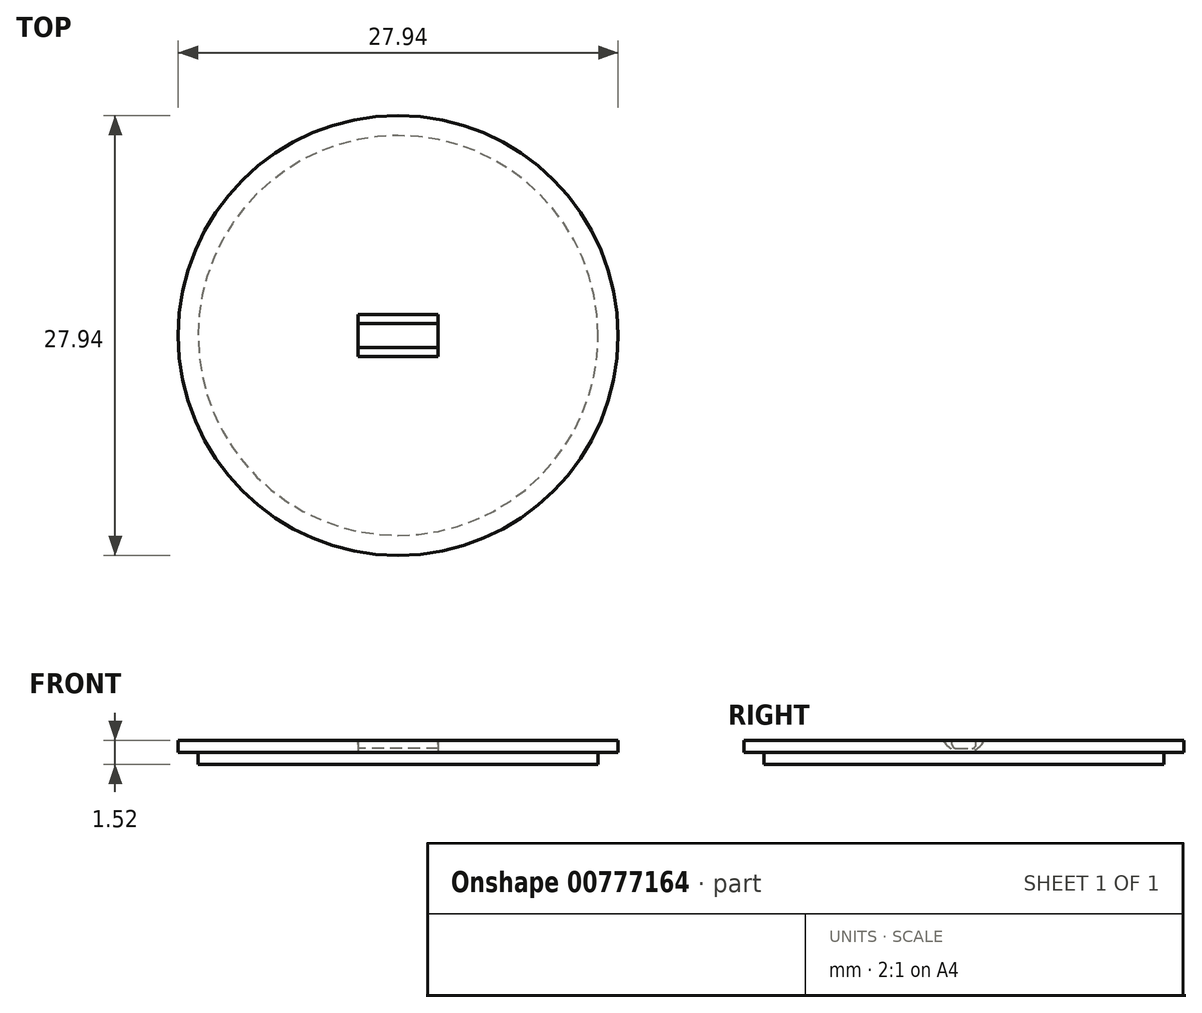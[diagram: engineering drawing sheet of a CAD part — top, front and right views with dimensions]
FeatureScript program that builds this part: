
annotation { "Feature Type Name" : "Feature", "Feature Type Description" : "" }
export const myFeature = defineFeature(function(context is Context, id is Id, definition is map)
    precondition{}
    {
        {
            var Q0;
            Q0=qCreatedBy(makeId("Top.planeOp"),FACE);
            var sketch = newSketch(context, id + "F0", { "sketchPlane" : qUnion([Q0])});
            skCircle(sketch, "E0", {"center": v(0, 0) * mm, "radius": 12.7 * mm});
            skSolve(sketch);
        }
        {
            var Q0;
            Q0=qSketchRegion(id+"F0",true);
            extrude(context, id + "F1", {"entities" : qUnion([Q0]), "oppositeDirection" : true, "depth" : 1.52 * mm, "offsetDistance" : 25.4 * mm});
        }
        {
            var Q0;
            Q0=qCreatedBy(makeId("Top.planeOp"),FACE);
            var sketch = newSketch(context, id + "F2", { "sketchPlane" : qUnion([Q0])});
            skCircle(sketch, "E1", {"center": v(0, 0) * mm, "radius": 13.97 * mm});
            skSolve(sketch);
        }
        {
            var Q0;
            Q0=qSketchRegion(id+"F2",true);
            extrude(context, id + "F3", {"entities" : qUnion([Q0]), "operationType" : NewBodyOperationType.ADD, "oppositeDirection" : true, "depth" : 0.76 * mm, "offsetDistance" : 25.4 * mm});
        }
        {
            var Q0;
            Q0=qCreatedBy(makeId("Front.planeOp"),FACE);
            var sketch = newSketch(context, id + "F4", { "sketchPlane" : qUnion([Q0])});
            skLineSegment(sketch, "E2.bottom", {"start": v(2.54, -0.76) * mm, "end": v(-2.54, -0.76) * mm});
            skLineSegment(sketch, "E2.top", {"start": v(2.54, 0.76) * mm, "end": v(-2.54, 0.76) * mm});
            skLineSegment(sketch, "E2.left", {"start": v(2.54, -0.76) * mm, "end": v(2.54, 0.76) * mm});
            skLineSegment(sketch, "E2.right", {"start": v(-2.54, -0.76) * mm, "end": v(-2.54, 0.76) * mm});
            skPoint(sketch, "E2.middle", {"position": v(0, 0) * mm});
            skSolve(sketch);
        }
        {
            var Q0;
            Q0=qSketchRegion(id+"F4",true);
            var Q1;
            Q1=sQuery(id+"F4.wireOp",EDGE,"E2.top");
            revolve(context, id + "F5", {"operationType" : NewBodyOperationType.REMOVE, "surfaceOperationType" : NewSurfaceOperationType.NEW, "entities" : qUnion([Q0]), "axis" : qUnion([Q1]), "revolveType" : RevolveType.FULL, "oppositeDirection" : true});
        }
        {
            var Q0;
            Q0=qCreatedBy(makeId("Top.planeOp"),FACE);
            var sketch = newSketch(context, id + "F6", { "sketchPlane" : qUnion([Q0])});
            skLineSegment(sketch, "E3.bottom", {"start": v(2.54, -0.76) * mm, "end": v(-2.54, -0.76) * mm});
            skLineSegment(sketch, "E3.top", {"start": v(2.54, 0.76) * mm, "end": v(-2.54, 0.76) * mm});
            skLineSegment(sketch, "E3.left", {"start": v(2.54, -0.76) * mm, "end": v(2.54, 0.76) * mm});
            skLineSegment(sketch, "E3.right", {"start": v(-2.54, -0.76) * mm, "end": v(-2.54, 0.76) * mm});
            skPoint(sketch, "E3.middle", {"position": v(0, 0) * mm});
            skSolve(sketch);
        }
        {
            var Q0;
            Q0=qSketchRegion(id+"F6",true);
            extrude(context, id + "F7", {"entities" : qUnion([Q0]), "oppositeDirection" : true, "depth" : 0.5 * mm, "offsetDistance" : 25.4 * mm});
        }
        {
            var Q0;
            Q0=makeQuery(id+"F7.opExtrude","CAP_EDGE",EDGE,{"disambiguationData":[OSD([sQuery(id+"F6.wireOp",EDGE,"E3.top")])],"isStart":false});
            var Q1;
            Q1=makeQuery(id+"F7.opExtrude","CAP_EDGE",EDGE,{"disambiguationData":[OSD([sQuery(id+"F6.wireOp",EDGE,"E3.bottom")])],"isStart":false});
            fillet(context, id + "F8", {"entities" : qUnion([Q0, Q1]), "radius" : 0.25 * mm, "tangentPropagation" : true, "allowEdgeOverflow" : false});
        }
    });
